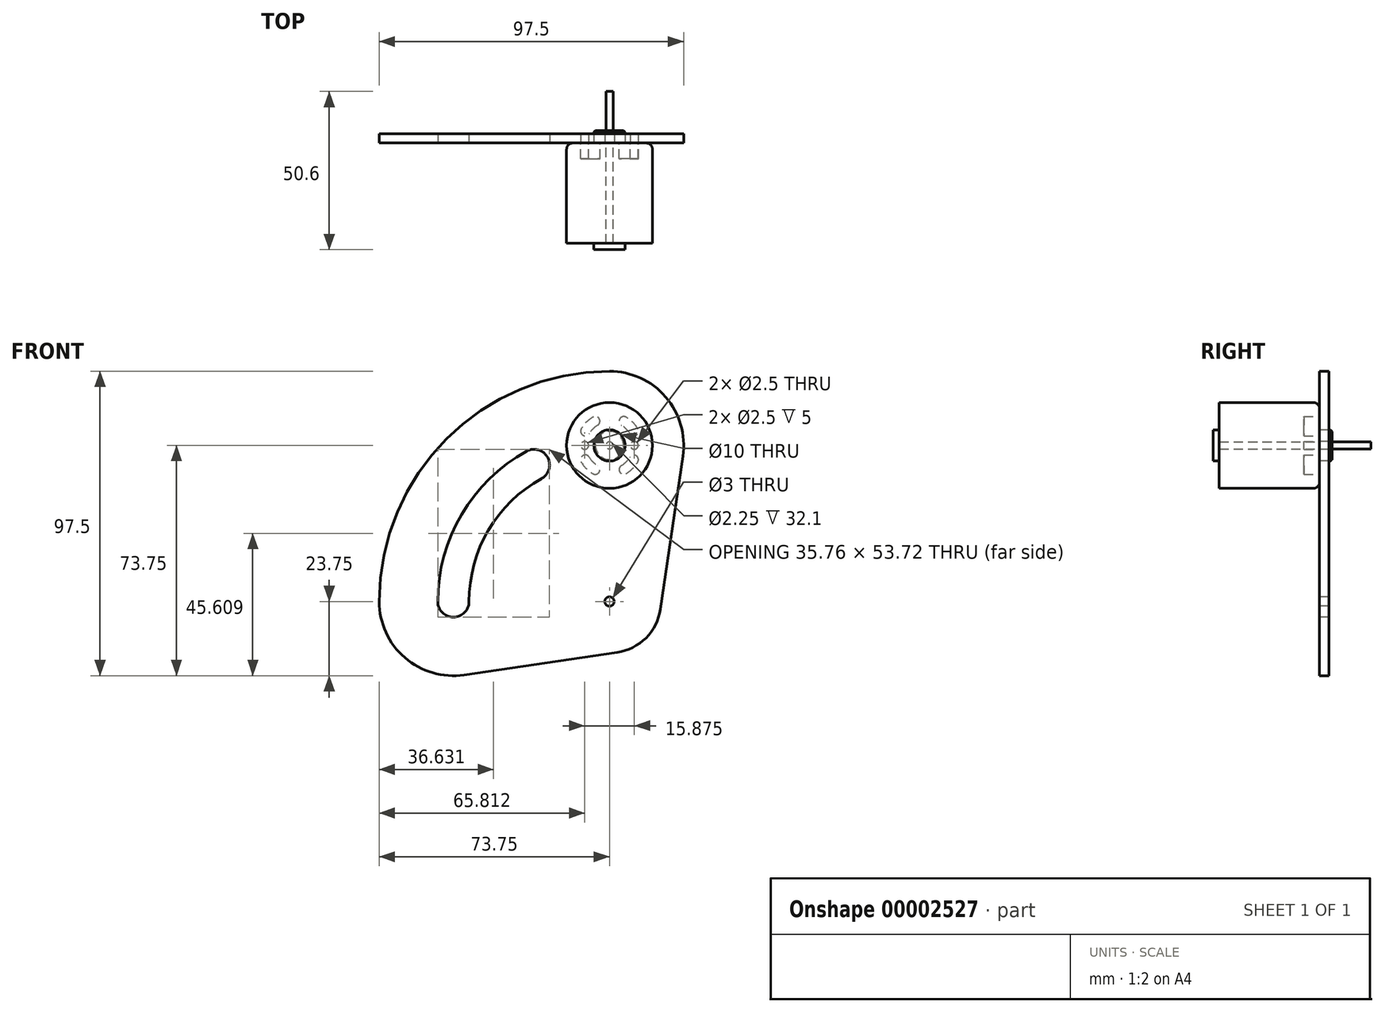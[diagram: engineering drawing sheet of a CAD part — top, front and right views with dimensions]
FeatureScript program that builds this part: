
annotation { "Feature Type Name" : "Feature", "Feature Type Description" : "" }
export const myFeature = defineFeature(function(context is Context, id is Id, definition is map)
    precondition{}
    {
        {
            var Q0;
            Q0=qCreatedBy(makeId("Front.planeOp"),FACE);
            var sketch = newSketch(context, id + "F0", { "sketchPlane" : qUnion([Q0])});
            skCircle(sketch, "E0", {"center": v(0, 0) * mm, "radius": 13.75 * mm});
            skCircle(sketch, "E1", {"center": v(0, 0) * mm, "radius": 5 * mm});
            skCircle(sketch, "E2", {"center": v(0, 0) * mm, "radius": 1.13 * mm});
            skSolve(sketch);
        }
        {
            var Q0;
            Q0 = qSketchRegion(id + "F0", true);
            var Q1;
            Q1=makeQuery(id+"F0.imprint","IMPRINT",FACE,{"disambiguationData":[TD([[makeQuery(id+"F0.imprint","IMPRINT",EDGE,{"derivedFrom":sQuery(id+"F0.wireOp",EDGE,"E1")}),1.0]])]});
            extrude(context, id + "F1", {"entities" : qUnion([Q0, Q1]), "depth" : 32.1 * mm});
        }
        {
            var Q0;
            Q0=makeQuery(id+"F1.opExtrude","CAP_FACE",FACE,{"disambiguationData":[OSD([sQuery(id+"F0.wireOp",EDGE,"E0"),sQuery(id+"F0.wireOp",EDGE,"E2")])],"isStart":false});
            var sketch = newSketch(context, id + "F2", { "sketchPlane" : qUnion([Q0])});
            skCircle(sketch, "E3", {"center": v(0, 0) * mm, "radius": 5 * mm});
            skSolve(sketch);
        }
        {
            var Q0;
            Q0=makeQuery(id+"F0.imprint","IMPRINT",FACE,{"disambiguationData":[TD([[makeQuery(id+"F0.imprint","IMPRINT",EDGE,{"derivedFrom":sQuery(id+"F0.wireOp",EDGE,"E1")}),1.0]])]});
            extrude(context, id + "F3", {"entities" : qUnion([Q0]), "operationType" : NewBodyOperationType.ADD, "oppositeDirection" : true, "depth" : 4 * mm});
        }
        {
            var Q0;
            Q0 = qSketchRegion(id + "F2", true);
            extrude(context, id + "F4", {"entities" : qUnion([Q0]), "operationType" : NewBodyOperationType.ADD, "depth" : 2 * mm});
        }
        {
            var Q0;
            Q0=makeQuery(id+"F0.imprint","IMPRINT",FACE,{"disambiguationData":[TD([[makeQuery(id+"F0.imprint","IMPRINT",EDGE,{"derivedFrom":sQuery(id+"F0.wireOp",EDGE,"E2")}),1.0]])]});
            extrude(context, id + "F5", {"entities" : qUnion([Q0]), "operationType" : NewBodyOperationType.ADD, "oppositeDirection" : true, "depth" : 16.5 * mm});
        }
        {
            var Q0;
            Q0=makeQuery(id+"F1.opExtrude","CAP_EDGE",EDGE,{"disambiguationData":[OSD([sQuery(id+"F0.wireOp",EDGE,"E0")])],"isStart":true});
            fillet(context, id + "F6", {"entities" : qUnion([Q0]), "radius" : 2 * mm, "tangentPropagation" : true, "allowEdgeOverflow" : false});
        }
        {
            var Q0;
            Q0=makeQuery(id+"F3.opExtrude","CAP_EDGE",EDGE,{"disambiguationData":[OSD([sQuery(id+"F0.wireOp",EDGE,"E1")])],"isStart":false});
            chamfer(context, id + "F7", {"entities" : qUnion([Q0]), "width" : .5 * mm, "tangentPropagation" : true});
        }
        {
            var Q0;
            Q0=makeQuery(id+"F0.imprint","IMPRINT",FACE,{"disambiguationData":[TD([[makeQuery(id+"F0.imprint","IMPRINT",EDGE,{"derivedFrom":sQuery(id+"F0.wireOp",EDGE,"E0")}),1.0]])]});
            var sketch = newSketch(context, id + "F8", { "sketchPlane" : qUnion([Q0])});
            skPoint(sketch, "E4.0", {"position": v(0, 0) * mm});
            skCircle(sketch, "E5", {"center": v(-7.94, 0) * mm, "radius": 1.25 * mm});
            skLineSegment(sketch, "E6", {"start": v(-7.94, 0) * mm, "end": v(7.94, 0) * mm, "construction": true});
            skCircle(sketch, "E7", {"center": v(7.94, 0) * mm, "radius": 1.25 * mm});
            skLineSegment(sketch, "E8", {"start": v(0, 0) * mm, "end": v(9.72, 9.72) * mm, "construction": true});
            skArc(sketch, "E9", {"start": v(7.42, 7.42) * mm, "mid": v(6.43, 8.3) * mm, "end": v(5.33, 9.05) * mm});
            skArc(sketch, "E10", {"start": v(5.3, 5.3) * mm, "mid": v(4.6, 5.93) * mm, "end": v(3.8, 6.46) * mm});
            skArc(sketch, "E11", {"start": v(5.33, 9.05) * mm, "mid": v(3.28, 8.51) * mm, "end": v(3.8, 6.46) * mm});
            skArc(sketch, "E12.MirrorCS", {"start": v(5.3, 5.3) * mm, "mid": v(5.93, 4.6) * mm, "end": v(6.46, 3.8) * mm});
            skArc(sketch, "E13.MirrorCS", {"start": v(9.05, 5.33) * mm, "mid": v(8.51, 3.28) * mm, "end": v(6.46, 3.8) * mm});
            skArc(sketch, "E14.MirrorCS", {"start": v(7.42, 7.42) * mm, "mid": v(8.3, 6.43) * mm, "end": v(9.05, 5.33) * mm});
            skArc(sketch, "E15.1.0", {"start": v(-7.42, 7.42) * mm, "mid": v(-8.3, 6.43) * mm, "end": v(-9.05, 5.33) * mm});
            skArc(sketch, "E15.1.1", {"start": v(-9.05, 5.33) * mm, "mid": v(-8.51, 3.28) * mm, "end": v(-6.46, 3.8) * mm});
            skArc(sketch, "E15.1.2", {"start": v(-5.3, 5.3) * mm, "mid": v(-5.93, 4.6) * mm, "end": v(-6.46, 3.8) * mm});
            skArc(sketch, "E15.1.3", {"start": v(-5.3, 5.3) * mm, "mid": v(-4.6, 5.93) * mm, "end": v(-3.8, 6.46) * mm});
            skArc(sketch, "E15.1.4", {"start": v(-7.42, 7.42) * mm, "mid": v(-6.43, 8.3) * mm, "end": v(-5.33, 9.05) * mm});
            skArc(sketch, "E15.1.5", {"start": v(-5.33, 9.05) * mm, "mid": v(-3.28, 8.51) * mm, "end": v(-3.8, 6.46) * mm});
            skArc(sketch, "E15.2.0", {"start": v(-7.42, -7.42) * mm, "mid": v(-6.43, -8.3) * mm, "end": v(-5.33, -9.05) * mm});
            skArc(sketch, "E15.2.1", {"start": v(-5.33, -9.05) * mm, "mid": v(-3.28, -8.51) * mm, "end": v(-3.8, -6.46) * mm});
            skArc(sketch, "E15.2.2", {"start": v(-5.3, -5.3) * mm, "mid": v(-4.6, -5.93) * mm, "end": v(-3.8, -6.46) * mm});
            skArc(sketch, "E15.2.3", {"start": v(-5.3, -5.3) * mm, "mid": v(-5.93, -4.6) * mm, "end": v(-6.46, -3.8) * mm});
            skArc(sketch, "E15.2.4", {"start": v(-7.42, -7.42) * mm, "mid": v(-8.3, -6.43) * mm, "end": v(-9.05, -5.33) * mm});
            skArc(sketch, "E15.2.5", {"start": v(-9.05, -5.33) * mm, "mid": v(-8.51, -3.28) * mm, "end": v(-6.46, -3.8) * mm});
            skArc(sketch, "E15.3.0", {"start": v(7.42, -7.42) * mm, "mid": v(8.3, -6.43) * mm, "end": v(9.05, -5.33) * mm});
            skArc(sketch, "E15.3.1", {"start": v(9.05, -5.33) * mm, "mid": v(8.51, -3.28) * mm, "end": v(6.46, -3.8) * mm});
            skArc(sketch, "E15.3.2", {"start": v(5.3, -5.3) * mm, "mid": v(5.93, -4.6) * mm, "end": v(6.46, -3.8) * mm});
            skArc(sketch, "E15.3.3", {"start": v(5.3, -5.3) * mm, "mid": v(4.6, -5.93) * mm, "end": v(3.8, -6.46) * mm});
            skArc(sketch, "E15.3.4", {"start": v(7.42, -7.42) * mm, "mid": v(6.43, -8.3) * mm, "end": v(5.33, -9.05) * mm});
            skArc(sketch, "E15.3.5", {"start": v(5.33, -9.05) * mm, "mid": v(3.28, -8.51) * mm, "end": v(3.8, -6.46) * mm});
            skSolve(sketch);
        }
        {
            var Q0;
            Q0=makeQuery(id+"F8.imprint","IMPRINT",FACE,{"disambiguationData":[TD([[makeQuery(id+"F8.imprint","IMPRINT",EDGE,{"derivedFrom":sQuery(id+"F8.wireOp",EDGE,"E7")}),1.0]])]});
            var Q1;
            Q1=makeQuery(id+"F8.imprint","IMPRINT",FACE,{"disambiguationData":[TD([[makeQuery(id+"F8.imprint","IMPRINT",EDGE,{"derivedFrom":sQuery(id+"F8.wireOp",EDGE,"E5")}),1.0]])]});
            var Q2;
            Q2=makeQuery(id+"F8.imprint","IMPRINT",FACE,{"disambiguationData":[TD([[makeQuery(id+"F8.imprint","IMPRINT",EDGE,{"derivedFrom":sQuery(id+"F8.wireOp",EDGE,"E15.1.0")}),1.0]])]});
            var Q3;
            Q3=makeQuery(id+"F8.imprint","IMPRINT",FACE,{"disambiguationData":[TD([[makeQuery(id+"F8.imprint","IMPRINT",EDGE,{"derivedFrom":sQuery(id+"F8.wireOp",EDGE,"E15.2.0")}),1.0]])]});
            var Q4;
            Q4=makeQuery(id+"F8.imprint","IMPRINT",FACE,{"disambiguationData":[TD([[makeQuery(id+"F8.imprint","IMPRINT",EDGE,{"derivedFrom":sQuery(id+"F8.wireOp",EDGE,"E15.3.0")}),1.0]])]});
            var Q5;
            Q5=makeQuery(id+"F8.imprint","IMPRINT",FACE,{"disambiguationData":[TD([[makeQuery(id+"F8.imprint","IMPRINT",EDGE,{"derivedFrom":sQuery(id+"F8.wireOp",EDGE,"E9")}),1.0]])]});
            var Q6;
            Q6=sQuery(id+"F8.wireOp",EDGE,"E6");
            var Q7;
            Q7=sQuery(id+"F8.wireOp",EDGE,"E5");
            extrude(context, id + "F9", {"entities" : qUnion([Q0, Q1, Q2, Q3, Q4, Q5]), "operationType" : NewBodyOperationType.REMOVE, "surfaceEntities" : qUnion([Q6, Q7]), "depth" : 5 * mm});
        }
        {
            var Q0;
            Q0=qCreatedBy(makeId("Front.planeOp"),FACE);
            var sketch = newSketch(context, id + "F10", { "sketchPlane" : qUnion([Q0])});
            skArc(sketch, "E16", {"start": v(23.5, -3.44) * mm, "mid": v(17.97, 15.53) * mm, "end": v(0, 23.75) * mm});
            skCircle(sketch, "E17", {"center": v(0, -50) * mm, "radius": 1.5 * mm});
            skArc(sketch, "E18", {"start": v(2.4, -66.33) * mm, "mid": v(11.67, -61.67) * mm, "end": v(16.33, -52.4) * mm});
            skLineSegment(sketch, "E19", {"start": v(23.5, -3.44) * mm, "end": v(16.33, -52.4) * mm});
            skCircle(sketch, "E20.0", {"center": v(0, 0) * mm, "radius": 5 * mm});
            skCircle(sketch, "E21.0", {"center": v(-7.94, 0) * mm, "radius": 1.25 * mm});
            skCircle(sketch, "E21.1", {"center": v(7.94, 0) * mm, "radius": 1.25 * mm});
            skArc(sketch, "E22", {"start": v(0, 23.75) * mm, "mid": v(-52.15, 2.15) * mm, "end": v(-73.75, -50) * mm});
            skArc(sketch, "E23", {"start": v(-73.75, -50) * mm, "mid": v(-65.53, -67.97) * mm, "end": v(-46.56, -73.5) * mm});
            skCircle(sketch, "E24", {"center": v(-50, -50) * mm, "radius": 5 * mm, "construction": true});
            skLineSegment(sketch, "E25", {"start": v(2.4, -66.33) * mm, "end": v(-46.56, -73.5) * mm});
            skLineSegment(sketch, "E26", {"start": v(0, -50) * mm, "end": v(-50, -50) * mm, "construction": true});
            skLineSegment(sketch, "E27", {"start": v(0, -50) * mm, "end": v(0, 0) * mm, "construction": true});
            skArc(sketch, "E28", {"start": v(0, 0) * mm, "mid": v(-35.36, -14.64) * mm, "end": v(-50, -50) * mm, "construction": true});
            skLineSegment(sketch, "E29", {"start": v(0, -50) * mm, "end": v(-24.2, -6.25) * mm, "construction": true});
            skArc(sketch, "E30", {"start": v(-26.63, -1.88) * mm, "mid": v(-47.38, -22.07) * mm, "end": v(-55, -50) * mm});
            skArc(sketch, "E31", {"start": v(-21.79, -10.63) * mm, "mid": v(-38.76, -27.15) * mm, "end": v(-45, -50) * mm});
            skArc(sketch, "E32", {"start": v(-21.79, -10.62) * mm, "mid": v(-19.83, -3.83) * mm, "end": v(-26.63, -1.87) * mm});
            skArc(sketch, "E33", {"start": v(-26.63, -1.87) * mm, "mid": v(-28.58, -8.67) * mm, "end": v(-21.79, -10.62) * mm, "construction": true});
            skArc(sketch, "E34", {"start": v(-55, -50) * mm, "mid": v(-50, -55) * mm, "end": v(-45, -50) * mm});
            skSolve(sketch);
        }
        {
            var Q0;
            Q0 = qSketchRegion(id + "F10", true);
            extrude(context, id + "F11", {"entities" : qUnion([Q0]), "oppositeDirection" : true, "depth" : 3 * mm});
        }
    });
